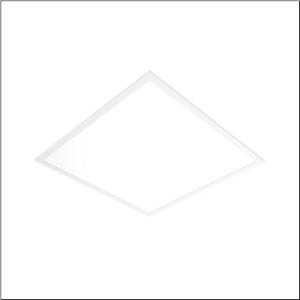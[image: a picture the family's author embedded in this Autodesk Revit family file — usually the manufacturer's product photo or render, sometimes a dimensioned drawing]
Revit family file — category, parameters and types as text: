
# Revit family: apollon_r__41_51mh12h72443_9ce2
name_source: partatom
category: Lighting Fixtures
units: mm (PartAtom-declared; Revit-internal decimal feet)

## family parameters
Cut with Voids When Loaded = No
Host = Face
Light Source = No
Part Type = Normal
Room Calculation Point = No
Round Connector Dimension = Use Diameter
Shared = No

## types (1)
- Apollon® 41 (1 x LED, 5000 lm, 38.5 W, 4000K)
    Apparent Load = 39 VA
    CIE Flux Codes = 61 87 97 100 100
    Color Rendering = 80
    Color Temperature = 4000K
    Default Elevation = 1800 mm
    Description = Apollon® 41, office luminaire, primary optical cover: prismatic diffuser, of PS, light emission: direct distribution, primary light characteristic: symmetric, installation type: lay-in mounting, LED, rated luminous flux: 5.000lm, luminous efficacy: 130lm/W, light colour: 840, colour temperature: 4000K, with terminal, 3-pole, mains connection: 220..240V, AC, 50/60Hz, rated input power: 38.5W, housing, of aluminium section, traffic white (RAL 9016), module: M600, length: 600mm, width: 600mm, height: 28mm, housing upper side, of sheet steel, protection rating (complete): IP20, protection rating (lamp compartment, on room side): IP40, insulation class (complete): insulation class II (safety insulation), certification: CE, ENEC, permissible operating ambient temperature: -25..+40°C, packaging unit: 1 piece
    Height = 0 mm  [stored 0 ft]
    Lamp = 1 x LED
    Lamp Light Flux = 5000 lm
    Lamp Power = 38.5 W
    Lamp count = 1
    Length = 600 mm
    Luminous efficacy = 130 lm/W
    Manufacturer = Siteco
    ModVariant = No
    Model = 51MH12H72443
    Mounting Place = Ceiling
    Mounting Type = Recessed
    Number of Poles = 1
    OnlyDefault = Yes
    Power Factor = 1
    Product Name = Apollon® 41
    Product group = office luminaire | ceiling recessed
    ProductGroupID = 401
    Protection Class = Protection class II
    Protection Degree = IP 20
    RLX_Detail_Level = 1
    RLX_Emergency_Light_Flux = 0 lm
    RLX_Emergency_Type = 0
    RLX_Emergency_Type_DB = No
    RlxData = <blob elided: 12201 chars, md5=dceb65e5>
    Socket = socket
    Standby Power = 0 W
    System Light Flux = 5000 lm
    System Power = 39 W
    Type Comments = Product without accessories
    Type Image = l_1291024.jpg
    URL = http://relux.com
    VarID = ---
    Voltage = 0 V
    Weight = 0.00 kg
    Width = 600 mm

note: [stored X ft] marks values corroborated as IEEE doubles in the binary element streams (Revit-internal decimal feet)

## geometry (parser evidence)
native form markers: Sweep x9
no freeform markers — native parametric forms only
